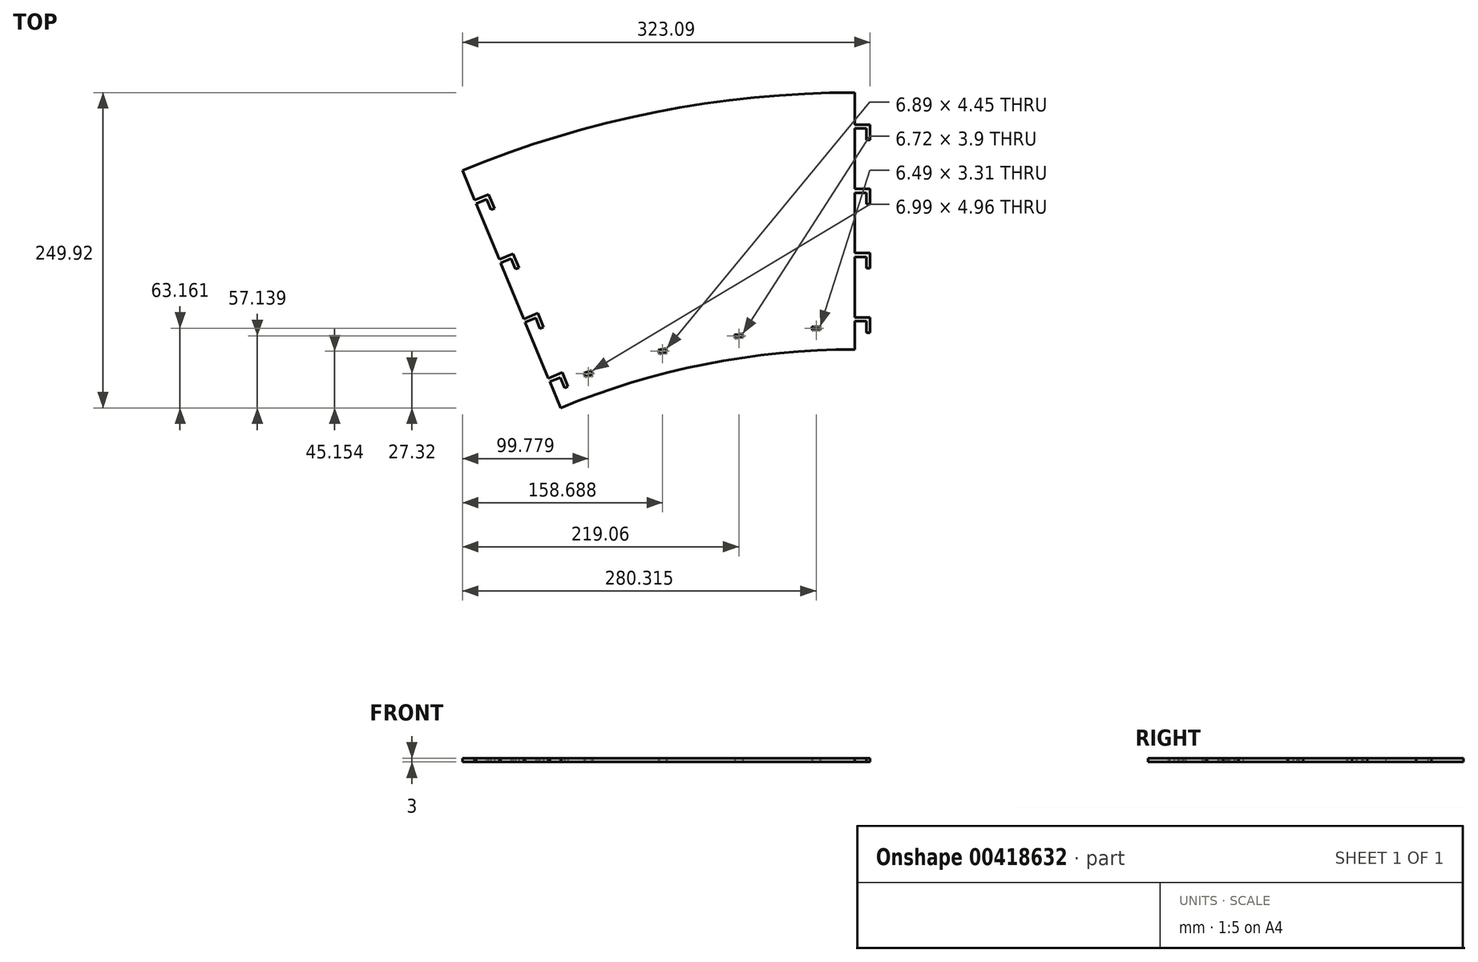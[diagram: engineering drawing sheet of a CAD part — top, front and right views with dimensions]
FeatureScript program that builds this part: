
annotation { "Feature Type Name" : "Feature", "Feature Type Description" : "" }
export const myFeature = defineFeature(function(context is Context, id is Id, definition is map)
    precondition{}
    {
        {
            var Q0;
            Q0=qCreatedBy(makeId("Top.planeOp"),FACE);
            var sketch = newSketch(context, id + "F0", { "sketchPlane" : qUnion([Q0])});
            skLineSegment(sketch, "E0", {"start": v(0, 0) * mm, "end": v(0, 610.8) * mm, "construction": true});
            skArc(sketch, "E1", {"start": v(0, 610.8) * mm, "mid": v(-118.94, 599.1) * mm, "end": v(-233.32, 564.48) * mm});
            skLineSegment(sketch, "E2", {"start": v(-311.1, 752.64) * mm, "end": v(0, 0) * mm, "construction": true});
            skArc(sketch, "E3", {"start": v(0, 814.4) * mm, "mid": v(-158.58, 798.81) * mm, "end": v(-311.1, 752.64) * mm});
            skLineSegment(sketch, "E4", {"start": v(-233.32, 564.48) * mm, "end": v(-311.1, 752.64) * mm});
            skLineSegment(sketch, "E5", {"start": v(0, 814.4) * mm, "end": v(-311.1, 814.4) * mm, "construction": true});
            skLineSegment(sketch, "E6", {"start": v(-311.1, 814.4) * mm, "end": v(-311.1, 564.48) * mm, "construction": true});
            skLineSegment(sketch, "E7", {"start": v(-311.1, 564.48) * mm, "end": v(0, 564.48) * mm, "construction": true});
            skLineSegment(sketch, "E8", {"start": v(0, 814.4) * mm, "end": v(0, 610.8) * mm});
            skLineSegment(sketch, "E9.1.0", {"start": v(-273.86, 766.97) * mm, "end": v(0, 0) * mm, "construction": true});
            skLineSegment(sketch, "E9.anchor1", {"start": v(0, 0) * mm, "end": v(-311.1, 752.64) * mm, "construction": true});
            skLineSegment(sketch, "E9.anchor2", {"start": v(0, 0) * mm, "end": v(-273.86, 766.97) * mm, "construction": true});
            skPoint(sketch, "E10", {"position": v(-211.31, 591.8) * mm});
            skLineSegment(sketch, "E11.bottom", {"start": v(-208.83, 594.28) * mm, "end": v(-214.8, 592.15) * mm});
            skLineSegment(sketch, "E11.top", {"start": v(-207.82, 591.46) * mm, "end": v(-213.8, 589.32) * mm});
            skLineSegment(sketch, "E11.left", {"start": v(-208.83, 594.28) * mm, "end": v(-207.82, 591.46) * mm});
            skLineSegment(sketch, "E11.right", {"start": v(-214.8, 592.15) * mm, "end": v(-213.8, 589.32) * mm});
            skLineSegment(sketch, "E12.1.0", {"start": v(-155.85, 610.32) * mm, "end": v(-155.12, 607.4) * mm});
            skLineSegment(sketch, "E12.1.1", {"start": v(-148.96, 608.95) * mm, "end": v(-155.12, 607.4) * mm});
            skLineSegment(sketch, "E12.1.2", {"start": v(-149.69, 611.86) * mm, "end": v(-155.85, 610.32) * mm});
            skLineSegment(sketch, "E12.1.3", {"start": v(-149.69, 611.86) * mm, "end": v(-148.96, 608.95) * mm});
            skLineSegment(sketch, "E12.2.0", {"start": v(-95.4, 622.64) * mm, "end": v(-94.95, 619.67) * mm});
            skLineSegment(sketch, "E12.2.1", {"start": v(-88.67, 620.6) * mm, "end": v(-94.95, 619.67) * mm});
            skLineSegment(sketch, "E12.2.2", {"start": v(-89.1, 623.57) * mm, "end": v(-95.4, 622.64) * mm});
            skLineSegment(sketch, "E12.2.3", {"start": v(-89.1, 623.57) * mm, "end": v(-88.67, 620.6) * mm});
            skLineSegment(sketch, "E12.3.0", {"start": v(-34.02, 628.98) * mm, "end": v(-33.87, 625.99) * mm});
            skLineSegment(sketch, "E12.3.1", {"start": v(-27.53, 626.3) * mm, "end": v(-33.87, 625.99) * mm});
            skLineSegment(sketch, "E12.3.2", {"start": v(-27.68, 629.3) * mm, "end": v(-34.02, 628.98) * mm});
            skLineSegment(sketch, "E12.3.3", {"start": v(-27.68, 629.3) * mm, "end": v(-27.53, 626.3) * mm});
            skLineSegment(sketch, "E12.4.0", {"start": v(27.68, 629.3) * mm, "end": v(27.53, 626.3) * mm});
            skLineSegment(sketch, "E12.4.1", {"start": v(33.87, 625.99) * mm, "end": v(27.53, 626.3) * mm});
            skLineSegment(sketch, "E12.4.2", {"start": v(34.02, 628.98) * mm, "end": v(27.68, 629.3) * mm});
            skLineSegment(sketch, "E12.4.3", {"start": v(34.02, 628.98) * mm, "end": v(33.87, 625.99) * mm});
            skLineSegment(sketch, "E12.anchor1", {"start": v(0, 0) * mm, "end": v(-214.8, 592.15) * mm, "construction": true});
            skLineSegment(sketch, "E12.anchor2", {"start": v(0, 0) * mm, "end": v(27.68, 629.3) * mm, "construction": true});
            skSolve(sketch);
        }
        {
            var Q0;
            Q0=makeQuery(id+"F0.imprint","IMPRINT",FACE,{"disambiguationData":[TD([[makeQuery(id+"F0.imprint","IMPRINT",EDGE,{"derivedFrom":sQuery(id+"F0.wireOp",EDGE,"E1")}),-1.0]])]});
            var sketch = newSketch(context, id + "F1", { "sketchPlane" : qUnion([Q0])});
            skPoint(sketch, "E13.0", {"position": v(0, 610.8) * mm});
            skPoint(sketch, "E14.0.1.0", {"position": v(0, 617.16) * mm});
            skPoint(sketch, "E14.0.2.0", {"position": v(0, 623.52) * mm});
            skPoint(sketch, "E14.0.3.0", {"position": v(0, 629.88) * mm});
            skPoint(sketch, "E14.0.4.0", {"position": v(0, 636.24) * mm});
            skPoint(sketch, "E14.0.5.0", {"position": v(0, 642.6) * mm});
            skPoint(sketch, "E14.0.6.0", {"position": v(0, 648.97) * mm});
            skPoint(sketch, "E14.0.7.0", {"position": v(0, 655.33) * mm});
            skPoint(sketch, "E14.0.8.0", {"position": v(0, 661.7) * mm});
            skPoint(sketch, "E14.0.9.0", {"position": v(0, 668.06) * mm});
            skPoint(sketch, "E14.0.10.0", {"position": v(0, 674.42) * mm});
            skPoint(sketch, "E14.0.11.0", {"position": v(0, 680.78) * mm});
            skPoint(sketch, "E14.0.12.0", {"position": v(0, 687.15) * mm});
            skPoint(sketch, "E14.0.13.0", {"position": v(0, 693.5) * mm});
            skPoint(sketch, "E14.0.14.0", {"position": v(0, 699.87) * mm});
            skPoint(sketch, "E14.0.15.0", {"position": v(0, 706.23) * mm});
            skPoint(sketch, "E14.0.16.0", {"position": v(0, 712.6) * mm});
            skLineSegment(sketch, "E14.direction1", {"start": v(0, 610.8) * mm, "end": v(25.4, 610.8) * mm, "construction": true});
            skLineSegment(sketch, "E14.direction2", {"start": v(0, 610.8) * mm, "end": v(0, 617.16) * mm, "construction": true});
            skPoint(sketch, "E15.center", {"position": v(0, 0) * mm});
            skPoint(sketch, "E16.0.0.17", {"position": v(0, 718.96) * mm});
            skPoint(sketch, "E16.0.0.18", {"position": v(0, 725.32) * mm});
            skPoint(sketch, "E16.0.0.19", {"position": v(0, 731.69) * mm});
            skPoint(sketch, "E16.0.0.20", {"position": v(0, 738.05) * mm});
            skPoint(sketch, "E16.0.0.21", {"position": v(0, 744.41) * mm});
            skPoint(sketch, "E16.0.0.22", {"position": v(0, 750.77) * mm});
            skPoint(sketch, "E16.0.0.23", {"position": v(0, 757.14) * mm});
            skPoint(sketch, "E16.0.0.24", {"position": v(0, 763.5) * mm});
            skPoint(sketch, "E16.0.0.25", {"position": v(0, 769.86) * mm});
            skPoint(sketch, "E16.0.0.26", {"position": v(0, 776.22) * mm});
            skPoint(sketch, "E16.0.0.27", {"position": v(0, 782.59) * mm});
            skPoint(sketch, "E16.0.0.28", {"position": v(0, 788.95) * mm});
            skPoint(sketch, "E16.0.0.29", {"position": v(0, 795.31) * mm});
            skPoint(sketch, "E16.0.0.30", {"position": v(0, 801.67) * mm});
            skPoint(sketch, "E16.0.0.31", {"position": v(0, 808.04) * mm});
            skPoint(sketch, "E16.0.0.32", {"position": v(0, 814.4) * mm});
            skLineSegment(sketch, "E17.0", {"start": v(0, 814.4) * mm, "end": v(-311.1, 814.4) * mm, "construction": true});
            skArc(sketch, "E18.0", {"start": v(0, 814.4) * mm, "mid": v(-158.58, 798.81) * mm, "end": v(-311.1, 752.64) * mm, "construction": true});
            skLineSegment(sketch, "E19", {"start": v(0, 814.4) * mm, "end": v(0, 808.04) * mm});
            skLineSegment(sketch, "E20", {"start": v(0, 808.04) * mm, "end": v(0, 801.67) * mm});
            skLineSegment(sketch, "E21", {"start": v(0, 801.67) * mm, "end": v(0, 795.31) * mm});
            skLineSegment(sketch, "E22", {"start": v(0, 795.31) * mm, "end": v(0, 788.95) * mm});
            skLineSegment(sketch, "E23", {"start": v(0, 788.95) * mm, "end": v(0, 782.59) * mm});
            skLineSegment(sketch, "E24", {"start": v(0, 776.22) * mm, "end": v(0, 769.86) * mm});
            skLineSegment(sketch, "E25", {"start": v(0, 769.86) * mm, "end": v(0, 763.5) * mm});
            skLineSegment(sketch, "E26", {"start": v(0, 763.5) * mm, "end": v(0, 757.14) * mm});
            skLineSegment(sketch, "E27", {"start": v(0, 757.14) * mm, "end": v(0, 750.77) * mm});
            skLineSegment(sketch, "E28", {"start": v(0, 750.77) * mm, "end": v(0, 744.41) * mm});
            skLineSegment(sketch, "E29", {"start": v(0, 738.05) * mm, "end": v(0, 731.69) * mm});
            skLineSegment(sketch, "E30", {"start": v(0, 731.69) * mm, "end": v(0, 725.32) * mm});
            skLineSegment(sketch, "E31", {"start": v(0, 725.32) * mm, "end": v(0, 718.96) * mm});
            skLineSegment(sketch, "E32", {"start": v(0, 718.96) * mm, "end": v(0, 712.6) * mm});
            skLineSegment(sketch, "E33", {"start": v(0, 712.6) * mm, "end": v(0, 706.23) * mm});
            skLineSegment(sketch, "E34", {"start": v(0, 699.87) * mm, "end": v(0, 693.5) * mm});
            skLineSegment(sketch, "E35", {"start": v(0, 693.5) * mm, "end": v(0, 687.15) * mm});
            skLineSegment(sketch, "E36", {"start": v(0, 687.15) * mm, "end": v(0, 680.78) * mm});
            skLineSegment(sketch, "E37", {"start": v(0, 680.78) * mm, "end": v(0, 674.42) * mm});
            skLineSegment(sketch, "E38", {"start": v(0, 674.42) * mm, "end": v(0, 668.06) * mm});
            skLineSegment(sketch, "E39", {"start": v(0, 661.7) * mm, "end": v(0, 655.33) * mm});
            skLineSegment(sketch, "E40", {"start": v(0, 655.33) * mm, "end": v(0, 648.97) * mm});
            skLineSegment(sketch, "E41", {"start": v(0, 648.97) * mm, "end": v(0, 642.6) * mm});
            skLineSegment(sketch, "E42", {"start": v(0, 642.6) * mm, "end": v(0, 636.24) * mm});
            skLineSegment(sketch, "E43", {"start": v(0, 636.24) * mm, "end": v(0, 629.88) * mm});
            skLineSegment(sketch, "E44", {"start": v(0, 623.52) * mm, "end": v(0, 617.16) * mm});
            skLineSegment(sketch, "E45", {"start": v(0, 617.16) * mm, "end": v(0, 610.8) * mm});
            skPoint(sketch, "E46.1.0", {"position": v(-3.45, 668.05) * mm});
            skPoint(sketch, "E46.1.1", {"position": v(-4, 776.21) * mm});
            skPoint(sketch, "E46.1.2", {"position": v(-3.77, 731.68) * mm});
            skPoint(sketch, "E46.1.3", {"position": v(-3.58, 693.5) * mm});
            skPoint(sketch, "E46.1.5", {"position": v(-3.35, 648.96) * mm});
            skPoint(sketch, "E46.1.6", {"position": v(-4.04, 782.58) * mm});
            skLineSegment(sketch, "E46.1.7", {"start": v(-3.6, 699.86) * mm, "end": v(-3.58, 693.5) * mm});
            skPoint(sketch, "E46.1.8", {"position": v(-3.25, 629.87) * mm});
            skLineSegment(sketch, "E46.1.9", {"start": v(-3.8, 738.04) * mm, "end": v(-3.77, 731.68) * mm});
            skPoint(sketch, "E46.1.10", {"position": v(-3.8, 738.04) * mm});
            skLineSegment(sketch, "E46.1.11", {"start": v(-3.97, 769.85) * mm, "end": v(-3.94, 763.49) * mm});
            skPoint(sketch, "E46.1.12", {"position": v(-3.6, 699.86) * mm});
            skPoint(sketch, "E46.1.14", {"position": v(-4.07, 788.94) * mm});
            skLineSegment(sketch, "E46.1.15", {"start": v(-3.18, 617.15) * mm, "end": v(-3.15, 610.79) * mm});
            skLineSegment(sketch, "E46.1.16", {"start": v(-3.31, 642.6) * mm, "end": v(-3.28, 636.24) * mm});
            skLineSegment(sketch, "E46.1.17", {"start": v(-3.7, 718.95) * mm, "end": v(-3.68, 712.59) * mm});
            skPoint(sketch, "E46.1.18", {"position": v(-3.41, 661.69) * mm});
            skLineSegment(sketch, "E46.1.19", {"start": v(-3.22, 623.51) * mm, "end": v(-3.18, 617.15) * mm});
            skPoint(sketch, "E46.1.20", {"position": v(-3.84, 744.4) * mm});
            skLineSegment(sketch, "E46.1.21", {"start": v(-4.07, 788.94) * mm, "end": v(-4.04, 782.58) * mm});
            skLineSegment(sketch, "E46.1.22", {"start": v(-3.64, 706.22) * mm, "end": v(-3.6, 699.86) * mm});
            skLineSegment(sketch, "E46.1.23", {"start": v(-3.9, 757.13) * mm, "end": v(-3.87, 750.76) * mm});
            skPoint(sketch, "E46.1.24", {"position": v(-4.1, 795.3) * mm});
            skPoint(sketch, "E46.1.26", {"position": v(-3.31, 642.6) * mm});
            skPoint(sketch, "E46.1.27", {"position": v(-3.48, 674.41) * mm});
            skLineSegment(sketch, "E46.1.28", {"start": v(-3.25, 629.87) * mm, "end": v(-3.22, 623.51) * mm});
            skPoint(sketch, "E46.1.29", {"position": v(-3.64, 706.22) * mm});
            skPoint(sketch, "E46.1.30", {"position": v(-3.87, 750.76) * mm});
            skLineSegment(sketch, "E46.1.31", {"start": v(-3.38, 655.32) * mm, "end": v(-3.35, 648.96) * mm});
            skPoint(sketch, "E46.1.32", {"position": v(-3.22, 623.51) * mm});
            skLineSegment(sketch, "E46.1.33", {"start": v(-3.68, 712.59) * mm, "end": v(-3.64, 706.22) * mm});
            skLineSegment(sketch, "E46.1.34", {"start": v(-4.2, 814.39) * mm, "end": v(-4.17, 808.03) * mm});
            skLineSegment(sketch, "E46.1.35", {"start": v(-3.84, 744.4) * mm, "end": v(-3.8, 738.04) * mm});
            skLineSegment(sketch, "E46.1.36", {"start": v(-3.41, 661.69) * mm, "end": v(-3.38, 655.32) * mm});
            skLineSegment(sketch, "E46.1.37", {"start": v(-3.28, 636.24) * mm, "end": v(-3.25, 629.87) * mm});
            skPoint(sketch, "E46.1.38", {"position": v(-3.9, 757.13) * mm});
            skPoint(sketch, "E46.1.39", {"position": v(-4.13, 801.66) * mm});
            skLineSegment(sketch, "E46.1.40", {"start": v(-4.1, 795.3) * mm, "end": v(-4.07, 788.94) * mm});
            skPoint(sketch, "E46.1.41", {"position": v(-3.51, 680.77) * mm});
            skPoint(sketch, "E46.1.42", {"position": v(-3.68, 712.59) * mm});
            skPoint(sketch, "E46.1.44", {"position": v(-3.38, 655.32) * mm});
            skLineSegment(sketch, "E46.1.45", {"start": v(-4.17, 808.03) * mm, "end": v(-4.13, 801.66) * mm});
            skLineSegment(sketch, "E46.1.46", {"start": v(-3.87, 750.76) * mm, "end": v(-3.84, 744.4) * mm});
            skLineSegment(sketch, "E46.1.47", {"start": v(-3.15, 610.79) * mm, "end": v(-3.18, 617.15) * mm, "construction": true});
            skLineSegment(sketch, "E46.1.48", {"start": v(-3.48, 674.41) * mm, "end": v(-3.45, 668.05) * mm});
            skPoint(sketch, "E46.1.49", {"position": v(-4.17, 808.03) * mm});
            skPoint(sketch, "E46.1.50", {"position": v(-3.7, 718.95) * mm});
            skPoint(sketch, "E46.1.51", {"position": v(-3.94, 763.49) * mm});
            skLineSegment(sketch, "E46.1.52", {"start": v(-3.51, 680.77) * mm, "end": v(-3.48, 674.41) * mm});
            skLineSegment(sketch, "E46.1.53", {"start": v(-3.77, 731.68) * mm, "end": v(-3.74, 725.31) * mm});
            skPoint(sketch, "E46.1.54", {"position": v(-3.28, 636.24) * mm});
            skPoint(sketch, "E46.1.55", {"position": v(-3.15, 610.79) * mm});
            skLineSegment(sketch, "E46.1.56", {"start": v(-4.04, 782.58) * mm, "end": v(-4, 776.21) * mm});
            skPoint(sketch, "E46.1.57", {"position": v(-3.54, 687.14) * mm});
            skLineSegment(sketch, "E46.1.59", {"start": v(-4, 776.21) * mm, "end": v(-3.97, 769.85) * mm});
            skLineSegment(sketch, "E46.1.60", {"start": v(-3.45, 668.05) * mm, "end": v(-3.41, 661.69) * mm});
            skPoint(sketch, "E46.1.61", {"position": v(-4.2, 814.39) * mm});
            skPoint(sketch, "E46.1.62", {"position": v(-3.74, 725.31) * mm});
            skPoint(sketch, "E46.1.63", {"position": v(-3.97, 769.85) * mm});
            skLineSegment(sketch, "E46.1.64", {"start": v(-3.58, 693.5) * mm, "end": v(-3.54, 687.14) * mm});
            skPoint(sketch, "E46.1.65", {"position": v(-3.18, 617.15) * mm});
            skLineSegment(sketch, "E46.anchor1", {"start": v(0, 0) * mm, "end": v(0, 610.8) * mm, "construction": true});
            skLineSegment(sketch, "E46.anchor2", {"start": v(0, 0) * mm, "end": v(-3.15, 610.79) * mm, "construction": true});
            skSolve(sketch);
        }
        {
            var Q0;
            Q0=qCreatedBy(makeId("Top.planeOp"),FACE);
            var sketch = newSketch(context, id + "F2", { "sketchPlane" : qUnion([Q0])});
            skLineSegment(sketch, "E47.0", {"start": v(0, 814.4) * mm, "end": v(0, 610.8) * mm, "construction": true});
            skPoint(sketch, "E48", {"position": v(0, 610.8) * mm});
            skPoint(sketch, "E49.0.1.0", {"position": v(0, 636.24) * mm});
            skPoint(sketch, "E49.0.2.0", {"position": v(0, 661.7) * mm});
            skPoint(sketch, "E49.0.3.0", {"position": v(0, 687.15) * mm});
            skPoint(sketch, "E49.0.4.0", {"position": v(0, 712.6) * mm});
            skLineSegment(sketch, "E49.direction1", {"start": v(0, 610.8) * mm, "end": v(25.4, 610.8) * mm, "construction": true});
            skLineSegment(sketch, "E49.direction2", {"start": v(0, 610.8) * mm, "end": v(0, 636.24) * mm, "construction": true});
            skPoint(sketch, "E50.0.0.5", {"position": v(0, 738.05) * mm});
            skPoint(sketch, "E50.0.0.6", {"position": v(0, 763.5) * mm});
            skPoint(sketch, "E50.0.0.7", {"position": v(0, 788.95) * mm});
            skPoint(sketch, "E50.0.0.8", {"position": v(0, 814.4) * mm});
            skLineSegment(sketch, "E51", {"start": v(0, 636.24) * mm, "end": v(12, 636.24) * mm});
            skLineSegment(sketch, "E52", {"start": v(12, 636.24) * mm, "end": v(12, 624.24) * mm});
            skLineSegment(sketch, "E53", {"start": v(12, 624.24) * mm, "end": v(9, 624.24) * mm});
            skLineSegment(sketch, "E54", {"start": v(9, 624.24) * mm, "end": v(9, 633.24) * mm});
            skLineSegment(sketch, "E55", {"start": v(9, 633.24) * mm, "end": v(0, 633.24) * mm});
            skLineSegment(sketch, "E56.0.1.0", {"start": v(9, 675.15) * mm, "end": v(9, 684.15) * mm});
            skLineSegment(sketch, "E56.0.1.1", {"start": v(12, 687.15) * mm, "end": v(12, 675.15) * mm});
            skLineSegment(sketch, "E56.0.1.2", {"start": v(9, 684.15) * mm, "end": v(0, 684.15) * mm});
            skLineSegment(sketch, "E56.0.1.3", {"start": v(0, 687.15) * mm, "end": v(12, 687.15) * mm});
            skLineSegment(sketch, "E56.0.1.5", {"start": v(12, 675.15) * mm, "end": v(9, 675.15) * mm});
            skLineSegment(sketch, "E56.0.2.0", {"start": v(9, 726.05) * mm, "end": v(9, 735.05) * mm});
            skLineSegment(sketch, "E56.0.2.1", {"start": v(12, 738.05) * mm, "end": v(12, 726.05) * mm});
            skLineSegment(sketch, "E56.0.2.2", {"start": v(9, 735.05) * mm, "end": v(0, 735.05) * mm});
            skLineSegment(sketch, "E56.0.2.3", {"start": v(0, 738.05) * mm, "end": v(12, 738.05) * mm});
            skLineSegment(sketch, "E56.0.2.5", {"start": v(12, 726.05) * mm, "end": v(9, 726.05) * mm});
            skLineSegment(sketch, "E56.0.3.0", {"start": v(9, 776.95) * mm, "end": v(9, 785.95) * mm});
            skLineSegment(sketch, "E56.0.3.1", {"start": v(12, 788.95) * mm, "end": v(12, 776.95) * mm});
            skLineSegment(sketch, "E56.0.3.2", {"start": v(9, 785.95) * mm, "end": v(0, 785.95) * mm});
            skLineSegment(sketch, "E56.0.3.3", {"start": v(0, 788.95) * mm, "end": v(12, 788.95) * mm});
            skLineSegment(sketch, "E56.0.3.5", {"start": v(12, 776.95) * mm, "end": v(9, 776.95) * mm});
            skLineSegment(sketch, "E56.direction1", {"start": v(0, 633.24) * mm, "end": v(25.4, 633.24) * mm, "construction": true});
            skLineSegment(sketch, "E56.direction2", {"start": v(0, 633.24) * mm, "end": v(0, 684.15) * mm, "construction": true});
            skLineSegment(sketch, "E57.1.0", {"start": v(-231.95, 592.58) * mm, "end": v(-227.37, 581.49) * mm});
            skPoint(sketch, "E57.1.1", {"position": v(-301.37, 729.12) * mm});
            skPoint(sketch, "E57.1.2", {"position": v(-281.93, 682.08) * mm});
            skLineSegment(sketch, "E57.1.3", {"start": v(-262.48, 635.04) * mm, "end": v(-251.4, 639.62) * mm});
            skPoint(sketch, "E57.1.4", {"position": v(-281.93, 682.08) * mm});
            skLineSegment(sketch, "E57.1.5", {"start": v(-272.46, 682.74) * mm, "end": v(-280.78, 679.3) * mm});
            skLineSegment(sketch, "E57.1.6", {"start": v(-253.02, 635.7) * mm, "end": v(-261.34, 632.26) * mm});
            skLineSegment(sketch, "E57.1.7", {"start": v(-270.84, 686.66) * mm, "end": v(-266.25, 675.57) * mm});
            skPoint(sketch, "E57.1.8", {"position": v(-301.37, 729.12) * mm});
            skLineSegment(sketch, "E57.1.9", {"start": v(-290.28, 733.7) * mm, "end": v(-285.7, 722.61) * mm});
            skLineSegment(sketch, "E57.1.10", {"start": v(-251.4, 639.62) * mm, "end": v(-246.8, 628.53) * mm});
            skLineSegment(sketch, "E57.1.11", {"start": v(-269.03, 674.43) * mm, "end": v(-272.46, 682.74) * mm});
            skLineSegment(sketch, "E57.1.12", {"start": v(-230.14, 580.34) * mm, "end": v(-233.58, 588.66) * mm});
            skLineSegment(sketch, "E57.1.13", {"start": v(-249.58, 627.39) * mm, "end": v(-253.02, 635.7) * mm});
            skLineSegment(sketch, "E57.1.14", {"start": v(-291.9, 729.79) * mm, "end": v(-300.22, 726.35) * mm});
            skLineSegment(sketch, "E57.1.15", {"start": v(-233.58, 588.66) * mm, "end": v(-241.9, 585.22) * mm});
            skLineSegment(sketch, "E57.1.16", {"start": v(-281.93, 682.08) * mm, "end": v(-270.84, 686.66) * mm});
            skLineSegment(sketch, "E57.1.17", {"start": v(-243.04, 588) * mm, "end": v(-231.95, 592.58) * mm});
            skLineSegment(sketch, "E57.1.18", {"start": v(-301.37, 729.12) * mm, "end": v(-290.28, 733.7) * mm});
            skLineSegment(sketch, "E57.1.19", {"start": v(-227.37, 581.49) * mm, "end": v(-230.14, 580.34) * mm});
            skLineSegment(sketch, "E57.1.20", {"start": v(-266.25, 675.57) * mm, "end": v(-269.03, 674.43) * mm});
            skPoint(sketch, "E57.1.21", {"position": v(-262.48, 635.04) * mm});
            skLineSegment(sketch, "E57.1.22", {"start": v(-246.8, 628.53) * mm, "end": v(-249.58, 627.39) * mm});
            skLineSegment(sketch, "E57.1.23", {"start": v(-285.7, 722.61) * mm, "end": v(-288.47, 721.47) * mm});
            skLineSegment(sketch, "E57.1.24", {"start": v(-288.47, 721.47) * mm, "end": v(-291.9, 729.79) * mm});
            skPoint(sketch, "E57.1.25", {"position": v(-262.48, 635.04) * mm});
            skPoint(sketch, "E57.1.26", {"position": v(-243.04, 588) * mm});
            skPoint(sketch, "E57.center", {"position": v(0, 0) * mm});
            skLineSegment(sketch, "E57.anchor1", {"start": v(0, 0) * mm, "end": v(0, 633.24) * mm, "construction": true});
            skLineSegment(sketch, "E57.anchor2", {"start": v(0, 0) * mm, "end": v(-241.9, 585.22) * mm, "construction": true});
            skLineSegment(sketch, "E58", {"start": v(0, 636.24) * mm, "end": v(0, 633.24) * mm});
            skLineSegment(sketch, "E59", {"start": v(0, 687.15) * mm, "end": v(0, 684.15) * mm});
            skLineSegment(sketch, "E60", {"start": v(0, 738.05) * mm, "end": v(0, 735.05) * mm});
            skLineSegment(sketch, "E61", {"start": v(0, 788.95) * mm, "end": v(0, 785.95) * mm});
            skLineSegment(sketch, "E62", {"start": v(-243.04, 588) * mm, "end": v(-241.9, 585.22) * mm});
            skLineSegment(sketch, "E63", {"start": v(-262.48, 635.04) * mm, "end": v(-261.34, 632.26) * mm});
            skLineSegment(sketch, "E64", {"start": v(-281.93, 682.08) * mm, "end": v(-280.78, 679.3) * mm});
            skLineSegment(sketch, "E65", {"start": v(-301.37, 729.12) * mm, "end": v(-300.22, 726.35) * mm});
            skSolve(sketch);
        }
        {
            var Q0;
            Q0=makeQuery(id+"F0.imprint","IMPRINT",FACE,{"disambiguationData":[TD([[makeQuery(id+"F0.imprint","IMPRINT",EDGE,{"derivedFrom":sQuery(id+"F0.wireOp",EDGE,"E1")}),-1.0]])]});
            extrude(context, id + "F3", {"entities" : qUnion([Q0]), "depth" : 3 * mm});
        }
        {
            var Q0;
            Q0=makeQuery(id+"F2.imprint","IMPRINT",FACE,{"disambiguationData":[TD([[makeQuery(id+"F2.imprint","IMPRINT",EDGE,{"derivedFrom":sQuery(id+"F2.wireOp",EDGE,"E56.0.3.0")}),-1.0]])]});
            var Q1;
            Q1=makeQuery(id+"F2.imprint","IMPRINT",FACE,{"disambiguationData":[TD([[makeQuery(id+"F2.imprint","IMPRINT",EDGE,{"derivedFrom":sQuery(id+"F2.wireOp",EDGE,"E56.0.2.0")}),-1.0]])]});
            var Q2;
            Q2=makeQuery(id+"F2.imprint","IMPRINT",FACE,{"disambiguationData":[TD([[makeQuery(id+"F2.imprint","IMPRINT",EDGE,{"derivedFrom":sQuery(id+"F2.wireOp",EDGE,"E51")}),-1.0]])]});
            var Q3;
            Q3=makeQuery(id+"F2.imprint","IMPRINT",FACE,{"disambiguationData":[TD([[makeQuery(id+"F2.imprint","IMPRINT",EDGE,{"derivedFrom":sQuery(id+"F2.wireOp",EDGE,"E56.0.1.0")}),-1.0]])]});
            extrude(context, id + "F4", {"entities" : qUnion([Q0, Q1, Q2, Q3]), "operationType" : NewBodyOperationType.ADD, "depth" : 3 * mm});
        }
        {
            var Q0;
            Q0=makeQuery(id+"F2.imprint","IMPRINT",FACE,{"disambiguationData":[TD([[makeQuery(id+"F2.imprint","IMPRINT",EDGE,{"derivedFrom":sQuery(id+"F2.wireOp",EDGE,"E57.1.0")}),-1.0]])]});
            var Q1;
            Q1=makeQuery(id+"F2.imprint","IMPRINT",FACE,{"disambiguationData":[TD([[makeQuery(id+"F2.imprint","IMPRINT",EDGE,{"derivedFrom":sQuery(id+"F2.wireOp",EDGE,"E57.1.9")}),-1.0]])]});
            var Q2;
            Q2=makeQuery(id+"F2.imprint","IMPRINT",FACE,{"disambiguationData":[TD([[makeQuery(id+"F2.imprint","IMPRINT",EDGE,{"derivedFrom":sQuery(id+"F2.wireOp",EDGE,"E57.1.3")}),-1.0]])]});
            var Q3;
            Q3=makeQuery(id+"F2.imprint","IMPRINT",FACE,{"disambiguationData":[TD([[makeQuery(id+"F2.imprint","IMPRINT",EDGE,{"derivedFrom":sQuery(id+"F2.wireOp",EDGE,"E57.1.5")}),-1.0]])]});
            extrude(context, id + "F5", {"entities" : qUnion([Q0, Q1, Q2, Q3]), "operationType" : NewBodyOperationType.REMOVE, "endBound" : BoundingType.THROUGH_ALL, "depth" : 25.4 * mm});
        }
    });
